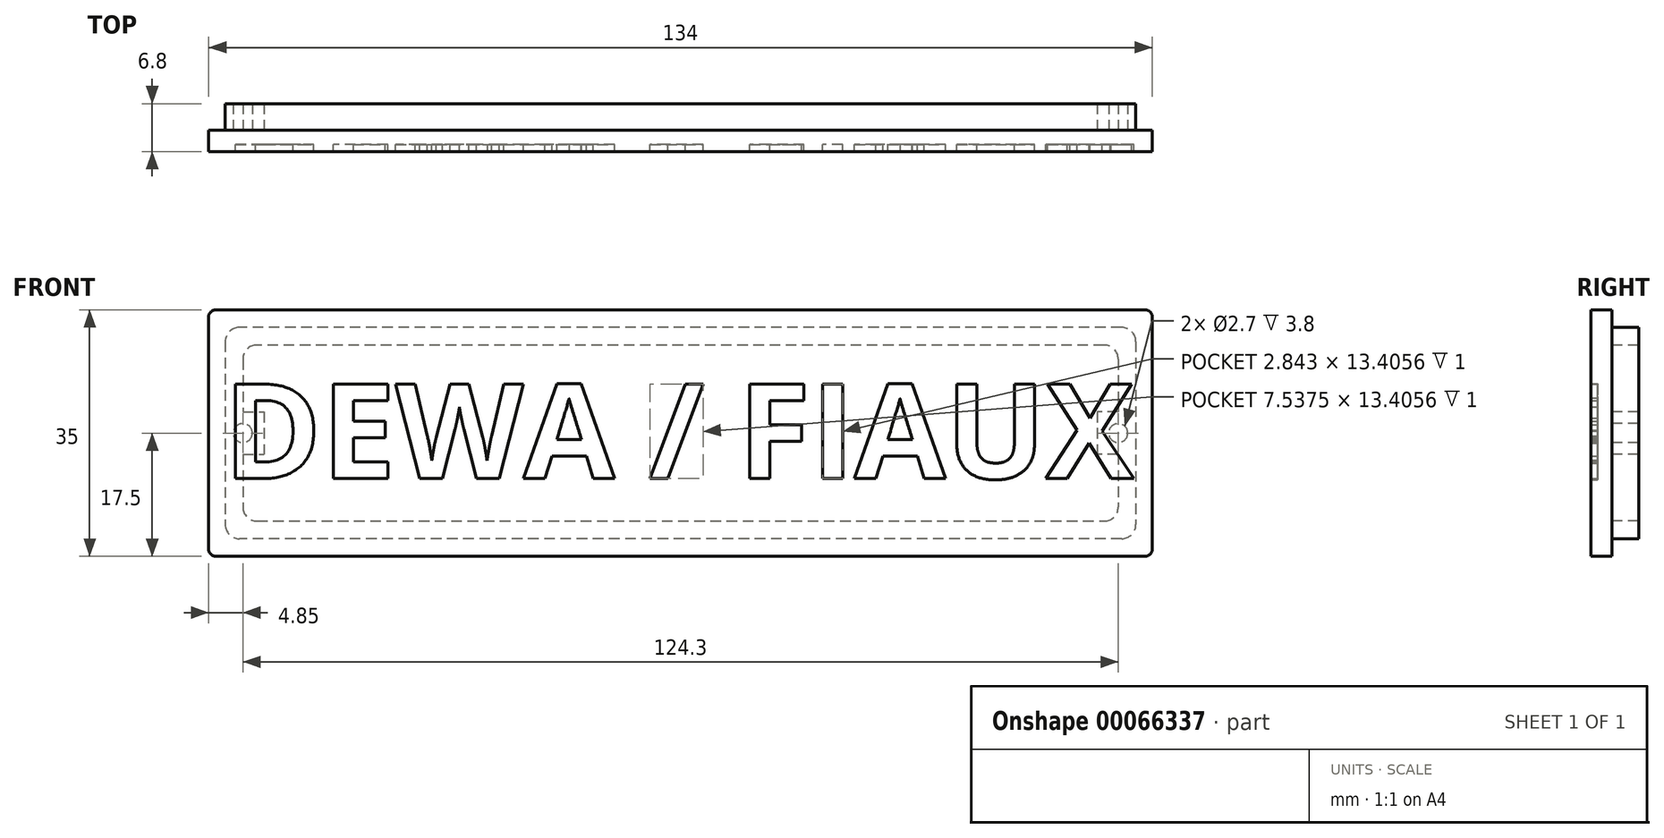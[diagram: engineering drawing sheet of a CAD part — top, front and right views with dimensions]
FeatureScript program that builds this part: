
annotation { "Feature Type Name" : "Feature", "Feature Type Description" : "" }
export const myFeature = defineFeature(function(context is Context, id is Id, definition is map)
    precondition{}
    {
        {
            var Q0;
            Q0=qCreatedBy(makeId("Front.planeOp"),FACE);
            var sketch = newSketch(context, id + "F0", { "sketchPlane" : qUnion([Q0])});
            skLineSegment(sketch, "E0.bottom", {"start": v(1, 0) * mm, "end": v(133, 0) * mm});
            skLineSegment(sketch, "E0.top", {"start": v(1, 35) * mm, "end": v(133, 35) * mm});
            skLineSegment(sketch, "E0.left", {"start": v(0, 1) * mm, "end": v(0, 34) * mm});
            skLineSegment(sketch, "E0.right", {"start": v(134, 1) * mm, "end": v(134, 34) * mm});
            skText(sketch, "E1", { "text": "DEWA / FIAUX", "fontName": "OpenSans-Bold.ttf"});
            skPoint(sketch, "E2.visualSharp", {"position": v(0, 35) * mm});
            skArc(sketch, "E2.filletArc", {"start": v(1, 35) * mm, "mid": v(0.3, 34.7) * mm, "end": v(0, 34) * mm});
            skPoint(sketch, "E3.visualSharp", {"position": v(0, 0) * mm});
            skArc(sketch, "E3.filletArc", {"start": v(0, 1) * mm, "mid": v(0.3, 0.3) * mm, "end": v(1, 0) * mm});
            skPoint(sketch, "E4.visualSharp", {"position": v(134, 0) * mm});
            skArc(sketch, "E4.filletArc", {"start": v(133, 0) * mm, "mid": v(133.7, 0.3) * mm, "end": v(134, 1) * mm});
            skPoint(sketch, "E5.visualSharp", {"position": v(134, 35) * mm});
            skArc(sketch, "E5.filletArc", {"start": v(134, 34) * mm, "mid": v(133.7, 34.7) * mm, "end": v(133, 35) * mm});
            const initialGuessF0  = {"E1": [0.00212, 0.01103, 1, 0, 0.01352]};
            skSetInitialGuess(sketch, initialGuessF0);
            skSolve(sketch);
        }
        {
            var Q0;
            Q0 = qSketchRegion(id + "F0", true);
            var Q1;
            Q1=makeQuery(id+"F0.imprint","IMPRINT",FACE,{"disambiguationData":[TD([[makeQuery(id+"F0.imprint","IMPRINT",EDGE,{"derivedFrom":sQuery(id+"F0.wireOp",EDGE,"E0.bottom")}),1.0]])]});
            var Q2;
            Q2=makeQuery(id+"F0.imprint","IMPRINT",FACE,{"disambiguationData":[TD([[makeQuery(id+"F0.imprint","IMPRINT",EDGE,{"derivedFrom":sQuery(id+"F0.wireOp",EDGE,"E1.sketch_text.stroke-7")}),1.0]])]});
            var Q3;
            Q3=makeQuery(id+"F0.imprint","IMPRINT",FACE,{"disambiguationData":[TD([[makeQuery(id+"F0.imprint","IMPRINT",EDGE,{"derivedFrom":sQuery(id+"F0.wireOp",EDGE,"E1.sketch_text.stroke-12")}),-1.0]])]});
            var Q4;
            Q4=makeQuery(id+"F0.imprint","IMPRINT",FACE,{"disambiguationData":[TD([[makeQuery(id+"F0.imprint","IMPRINT",EDGE,{"derivedFrom":sQuery(id+"F0.wireOp",EDGE,"E1.sketch_text.stroke-24")}),-1.0]])]});
            var Q5;
            Q5=makeQuery(id+"F0.imprint","IMPRINT",FACE,{"disambiguationData":[TD([[makeQuery(id+"F0.imprint","IMPRINT",EDGE,{"derivedFrom":sQuery(id+"F0.wireOp",EDGE,"E1.sketch_text.stroke-56")}),1.0]])]});
            var Q6;
            Q6=makeQuery(id+"F0.imprint","IMPRINT",FACE,{"disambiguationData":[TD([[makeQuery(id+"F0.imprint","IMPRINT",EDGE,{"derivedFrom":sQuery(id+"F0.wireOp",EDGE,"E1.sketch_text.stroke-60")}),-1.0]])]});
            var Q7;
            Q7=makeQuery(id+"F0.imprint","IMPRINT",FACE,{"disambiguationData":[TD([[makeQuery(id+"F0.imprint","IMPRINT",EDGE,{"derivedFrom":sQuery(id+"F0.wireOp",EDGE,"E1.sketch_text.stroke-64")}),-1.0]])]});
            var Q8;
            Q8=makeQuery(id+"F0.imprint","IMPRINT",FACE,{"disambiguationData":[TD([[makeQuery(id+"F0.imprint","IMPRINT",EDGE,{"derivedFrom":sQuery(id+"F0.wireOp",EDGE,"E1.sketch_text.stroke-74")}),-1.0]])]});
            var Q9;
            Q9=makeQuery(id+"F0.imprint","IMPRINT",FACE,{"disambiguationData":[TD([[makeQuery(id+"F0.imprint","IMPRINT",EDGE,{"derivedFrom":sQuery(id+"F0.wireOp",EDGE,"E1.sketch_text.stroke-90")}),-1.0]])]});
            var Q10;
            Q10=makeQuery(id+"F0.imprint","IMPRINT",FACE,{"disambiguationData":[TD([[makeQuery(id+"F0.imprint","IMPRINT",EDGE,{"derivedFrom":sQuery(id+"F0.wireOp",EDGE,"E1.sketch_text.stroke-86")}),1.0]])]});
            var Q11;
            Q11=makeQuery(id+"F0.imprint","IMPRINT",FACE,{"disambiguationData":[TD([[makeQuery(id+"F0.imprint","IMPRINT",EDGE,{"derivedFrom":sQuery(id+"F0.wireOp",EDGE,"E1.sketch_text.stroke-0")}),-1.0]])]});
            var Q12;
            Q12=makeQuery(id+"F0.imprint","IMPRINT",FACE,{"disambiguationData":[TD([[makeQuery(id+"F0.imprint","IMPRINT",EDGE,{"derivedFrom":sQuery(id+"F0.wireOp",EDGE,"E1.sketch_text.stroke-105")}),-1.0]])]});
            var Q13;
            Q13=makeQuery(id+"F0.imprint","IMPRINT",FACE,{"disambiguationData":[TD([[makeQuery(id+"F0.imprint","IMPRINT",EDGE,{"derivedFrom":sQuery(id+"F0.wireOp",EDGE,"E1.sketch_text.stroke-48")}),-1.0]])]});
            var Q14;
            Q14=makeQuery(id+"F0.imprint","IMPRINT",FACE,{"disambiguationData":[TD([[makeQuery(id+"F0.imprint","IMPRINT",EDGE,{"derivedFrom":sQuery(id+"F0.wireOp",EDGE,"E1.sketch_text.stroke-78")}),-1.0]])]});
            extrude(context, id + "F1", {"entities" : qUnion([Q0, Q1, Q2, Q3, Q4, Q5, Q6, Q7, Q8, Q9, Q10, Q11, Q12, Q13, Q14]), "oppositeDirection" : true, "depth" : 2 * mm});
        }
        {
            var Q0;
            Q0=makeQuery(id+"F0.imprint","IMPRINT",FACE,{"disambiguationData":[TD([[makeQuery(id+"F0.imprint","IMPRINT",EDGE,{"derivedFrom":sQuery(id+"F0.wireOp",EDGE,"E1.sketch_text.stroke-56")}),1.0]])]});
            var Q1;
            Q1=makeQuery(id+"F0.imprint","IMPRINT",FACE,{"disambiguationData":[TD([[makeQuery(id+"F0.imprint","IMPRINT",EDGE,{"derivedFrom":sQuery(id+"F0.wireOp",EDGE,"E1.sketch_text.stroke-86")}),1.0]])]});
            var Q2;
            Q2=makeQuery(id+"F0.imprint","IMPRINT",FACE,{"disambiguationData":[TD([[makeQuery(id+"F0.imprint","IMPRINT",EDGE,{"derivedFrom":sQuery(id+"F0.wireOp",EDGE,"E1.sketch_text.stroke-7")}),1.0]])]});
            var Q3;
            Q3=makeQuery(id+"F0.imprint","IMPRINT",FACE,{"disambiguationData":[TD([[makeQuery(id+"F0.imprint","IMPRINT",EDGE,{"derivedFrom":sQuery(id+"F0.wireOp",EDGE,"E0.bottom")}),1.0]])]});
            extrude(context, id + "F2", {"entities" : qUnion([Q0, Q1, Q2, Q3]), "operationType" : NewBodyOperationType.ADD, "depth" : 1 * mm});
        }
        {
            var Q0;
            Q0=makeQuery(id+"F1.opExtrude","CAP_FACE",FACE,{"disambiguationData":[OSD([sQuery(id+"F0.wireOp",EDGE,"E0.bottom"),sQuery(id+"F0.wireOp",EDGE,"E0.top"),sQuery(id+"F0.wireOp",EDGE,"E0.left"),sQuery(id+"F0.wireOp",EDGE,"E0.right")])],"isStart":false});
            var sketch = newSketch(context, id + "F3", { "sketchPlane" : qUnion([Q0])});
            skLineSegment(sketch, "E6", {"start": v(-134, 17.5) * mm, "end": v(0, 17.5) * mm, "construction": true});
            skLineSegment(sketch, "E7.bottom", {"start": v(-129.65, 32.5) * mm, "end": v(-4.35, 32.5) * mm});
            skLineSegment(sketch, "E7.top", {"start": v(-129.65, 2.5) * mm, "end": v(-4.35, 2.5) * mm});
            skLineSegment(sketch, "E7.left", {"start": v(-131.65, 30.5) * mm, "end": v(-131.65, 4.5) * mm});
            skLineSegment(sketch, "E7.right", {"start": v(-2.35, 30.5) * mm, "end": v(-2.35, 4.5) * mm});
            skLineSegment(sketch, "E8", {"start": v(-67, 35) * mm, "end": v(-67, 0) * mm, "construction": true});
            skPoint(sketch, "E9.visualSharp", {"position": v(-131.65, 32.5) * mm});
            skArc(sketch, "E9.filletArc", {"start": v(-129.65, 32.5) * mm, "mid": v(-131.06, 31.91) * mm, "end": v(-131.65, 30.5) * mm});
            skPoint(sketch, "E10.visualSharp", {"position": v(-131.65, 2.5) * mm});
            skArc(sketch, "E10.filletArc", {"start": v(-131.65, 4.5) * mm, "mid": v(-131.06, 3.09) * mm, "end": v(-129.65, 2.5) * mm});
            skPoint(sketch, "E11.visualSharp", {"position": v(-2.35, 2.5) * mm});
            skArc(sketch, "E11.filletArc", {"start": v(-4.35, 2.5) * mm, "mid": v(-2.94, 3.09) * mm, "end": v(-2.35, 4.5) * mm});
            skPoint(sketch, "E12.visualSharp", {"position": v(-2.35, 32.5) * mm});
            skArc(sketch, "E12.filletArc", {"start": v(-2.35, 30.5) * mm, "mid": v(-2.94, 31.91) * mm, "end": v(-4.35, 32.5) * mm});
            skLineSegment(sketch, "E13.1", {"start": v(-127.15, 30) * mm, "end": v(-67, 30) * mm});
            skLineSegment(sketch, "E13.2", {"start": v(-129.15, 28) * mm, "end": v(-129.15, 20.5) * mm});
            skLineSegment(sketch, "E13.3", {"start": v(-127.15, 5) * mm, "end": v(-67, 5) * mm});
            skPoint(sketch, "E14.visualSharp", {"position": v(-129.15, 30) * mm});
            skArc(sketch, "E14.filletArc", {"start": v(-127.15, 30) * mm, "mid": v(-128.56, 29.41) * mm, "end": v(-129.15, 28) * mm});
            skPoint(sketch, "E15.visualSharp", {"position": v(-129.15, 5) * mm});
            skArc(sketch, "E15.filletArc", {"start": v(-129.15, 7) * mm, "mid": v(-128.56, 5.59) * mm, "end": v(-127.15, 5) * mm});
            skLineSegment(sketch, "E16.bottom", {"start": v(-129.15, 20.5) * mm, "end": v(-126.15, 20.5) * mm});
            skLineSegment(sketch, "E16.top", {"start": v(-129.15, 14.5) * mm, "end": v(-126.15, 14.5) * mm});
            skLineSegment(sketch, "E16.left", {"start": v(-131.65, 20.5) * mm, "end": v(-131.65, 14.5) * mm});
            skLineSegment(sketch, "E16.right", {"start": v(-126.15, 20.5) * mm, "end": v(-126.15, 14.5) * mm});
            skCircle(sketch, "E17", {"center": v(-129.15, 17.5) * mm, "radius": 1.35 * mm});
            skLineSegment(sketch, "E18.trimOffspring", {"start": v(-129.15, 14.5) * mm, "end": v(-129.15, 7) * mm});
            skPoint(sketch, "E19", {"position": v(-67, 30) * mm});
            skPoint(sketch, "E20", {"position": v(-67, 5) * mm});
            skPoint(sketch, "E21.orphan", {"position": v(-6.85, 30) * mm});
            skPoint(sketch, "E22.orphan", {"position": v(-6.85, 5) * mm});
            skLineSegment(sketch, "E23.MirrorCS", {"start": v(-6.85, 30) * mm, "end": v(-67, 30) * mm});
            skArc(sketch, "E24.MirrorCS", {"start": v(-6.85, 30) * mm, "mid": v(-5.44, 29.41) * mm, "end": v(-4.85, 28) * mm});
            skLineSegment(sketch, "E25.MirrorCS", {"start": v(-4.85, 28) * mm, "end": v(-4.85, 20.5) * mm});
            skCircle(sketch, "E26.MirrorC", {"center": v(-4.85, 17.5) * mm, "radius": 1.35 * mm});
            skLineSegment(sketch, "E27.MirrorCS", {"start": v(-4.85, 20.5) * mm, "end": v(-7.85, 20.5) * mm});
            skLineSegment(sketch, "E28.MirrorCS", {"start": v(-7.85, 20.5) * mm, "end": v(-7.85, 14.5) * mm});
            skLineSegment(sketch, "E29.MirrorCS", {"start": v(-4.85, 14.5) * mm, "end": v(-7.85, 14.5) * mm});
            skLineSegment(sketch, "E30.MirrorCS", {"start": v(-4.85, 14.5) * mm, "end": v(-4.85, 7) * mm});
            skArc(sketch, "E31.MirrorCS", {"start": v(-4.85, 7) * mm, "mid": v(-5.44, 5.59) * mm, "end": v(-6.85, 5) * mm});
            skLineSegment(sketch, "E32.MirrorCS", {"start": v(-6.85, 5) * mm, "end": v(-67, 5) * mm});
            skSolve(sketch);
        }
        {
            var Q0;
            Q0 = qSketchRegion(id + "F3", true);
            extrude(context, id + "F4", {"entities" : qUnion([Q0]), "operationType" : NewBodyOperationType.ADD, "depth" : 3.8 * mm});
        }
    });
